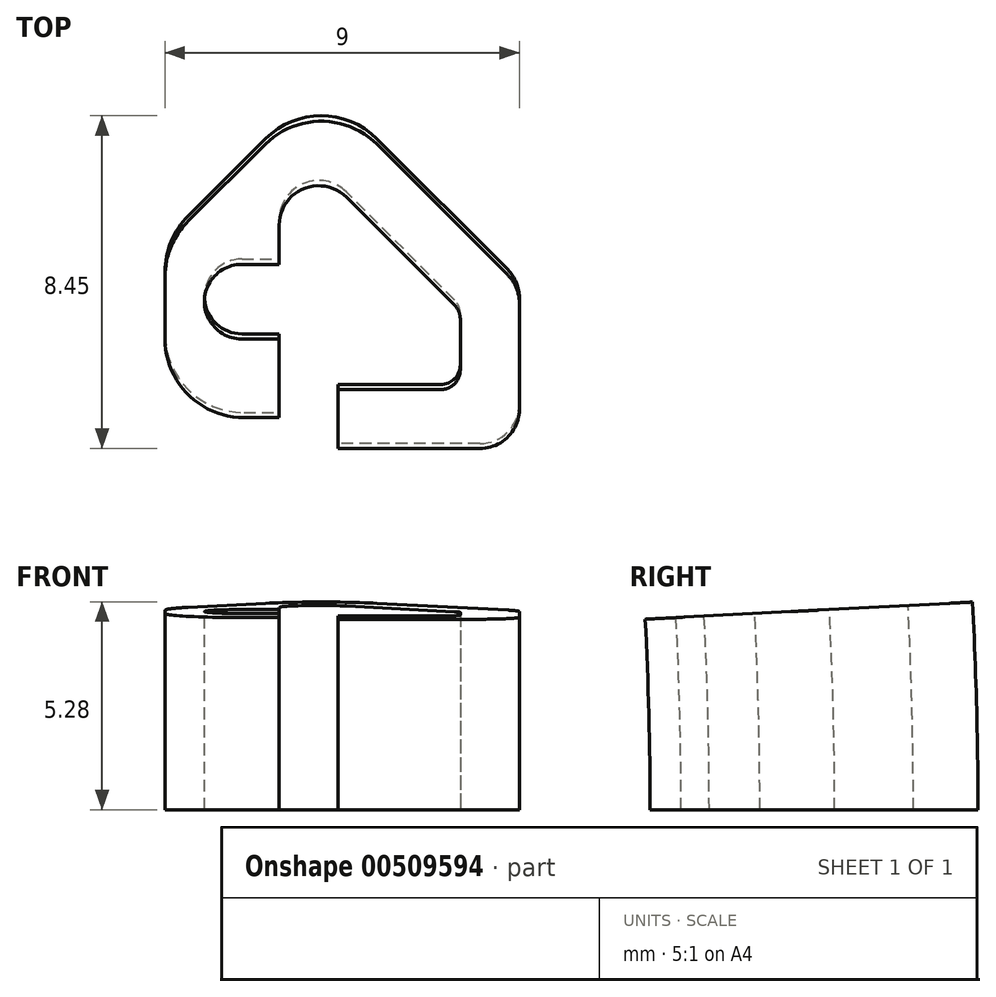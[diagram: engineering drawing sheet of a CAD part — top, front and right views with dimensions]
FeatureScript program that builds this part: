
annotation { "Feature Type Name" : "Feature", "Feature Type Description" : "" }
export const myFeature = defineFeature(function(context is Context, id is Id, definition is map)
    precondition{}
    {
        {
            var Q0;
            Q0=qCreatedBy(makeId("Top.planeOp"),FACE);
            var sketch = newSketch(context, id + "F0", { "sketchPlane" : qUnion([Q0])});
            skLineSegment(sketch, "E0", {"start": v(2.48, 100.21) * mm, "end": v(5.8, 96.89) * mm});
            skLineSegment(sketch, "E1", {"start": v(6.1, 96.18) * mm, "end": v(6.1, 93.47) * mm});
            skLineSegment(sketch, "E2", {"start": v(5.1, 92.47) * mm, "end": v(1.5, 92.47) * mm});
            skLineSegment(sketch, "E3", {"start": v(1.5, 92.47) * mm, "end": v(1.5, 93.97) * mm});
            skLineSegment(sketch, "E4", {"start": v(1.5, 93.97) * mm, "end": v(4.1, 93.97) * mm});
            skLineSegment(sketch, "E5", {"start": v(4.6, 94.47) * mm, "end": v(4.6, 95.77) * mm});
            skLineSegment(sketch, "E6", {"start": v(4.45, 96.12) * mm, "end": v(1.7, 98.87) * mm});
            skPoint(sketch, "E7.visualSharp", {"position": v(4.6, 93.97) * mm});
            skArc(sketch, "E7.filletArc", {"start": v(4.1, 93.97) * mm, "mid": v(4.45, 94.12) * mm, "end": v(4.6, 94.47) * mm});
            skPoint(sketch, "E8.visualSharp", {"position": v(4.6, 95.97) * mm});
            skArc(sketch, "E8.filletArc", {"start": v(4.6, 95.77) * mm, "mid": v(4.56, 95.96) * mm, "end": v(4.45, 96.12) * mm});
            skPoint(sketch, "E9.visualSharp", {"position": v(6.1, 92.47) * mm});
            skArc(sketch, "E9.filletArc", {"start": v(5.1, 92.47) * mm, "mid": v(5.8, 92.77) * mm, "end": v(6.1, 93.47) * mm});
            skPoint(sketch, "E10.visualSharp", {"position": v(6.1, 96.6) * mm});
            skArc(sketch, "E10.filletArc", {"start": v(6.1, 96.18) * mm, "mid": v(6.02, 96.56) * mm, "end": v(5.8, 96.89) * mm});
            skLineSegment(sketch, "E11", {"start": v(-2.9, 96.84) * mm, "end": v(-2.9, 95.26) * mm});
            skLineSegment(sketch, "E12", {"start": v(-0.9, 93.26) * mm, "end": v(0, 93.26) * mm});
            skLineSegment(sketch, "E13", {"start": v(0, 93.26) * mm, "end": v(0, 95.26) * mm});
            skArc(sketch, "E14", {"start": v(-0.95, 97.16) * mm, "mid": v(-1.9, 96.2) * mm, "end": v(-0.95, 95.26) * mm});
            skLineSegment(sketch, "E15", {"start": v(0, 97.16) * mm, "end": v(0, 95.26) * mm, "construction": true});
            skLineSegment(sketch, "E16", {"start": v(0, 95.26) * mm, "end": v(-0.95, 95.26) * mm});
            skPoint(sketch, "E17", {"position": v(-1.9, 96.2) * mm});
            skPoint(sketch, "E18.visualSharp", {"position": v(-2.9, 93.26) * mm});
            skArc(sketch, "E18.filletArc", {"start": v(-2.9, 95.26) * mm, "mid": v(-2.31, 93.85) * mm, "end": v(-0.9, 93.26) * mm});
            skPoint(sketch, "E19.visualSharp", {"position": v(-2.9, 102.7) * mm});
            skPoint(sketch, "E20.visualSharp", {"position": v(0, 102.7) * mm});
            skLineSegment(sketch, "E21", {"start": v(0, 0) * mm, "end": v(46.15, 0) * mm, "construction": true});
            skLineSegment(sketch, "E22", {"start": v(-0.95, 97.16) * mm, "end": v(0, 97.16) * mm});
            skLineSegment(sketch, "E23", {"start": v(0, 97.16) * mm, "end": v(0, 98.16) * mm});
            skPoint(sketch, "E24.visualSharp", {"position": v(0, 100.57) * mm});
            skArc(sketch, "E24.filletArc", {"start": v(1.7, 98.87) * mm, "mid": v(0.62, 99.08) * mm, "end": v(0, 98.16) * mm});
            skLineSegment(sketch, "E25", {"start": v(-0.35, 100.22) * mm, "end": v(-2.31, 98.26) * mm});
            skPoint(sketch, "E26.visualSharp", {"position": v(1.07, 101.63) * mm});
            skArc(sketch, "E26.filletArc", {"start": v(2.48, 100.21) * mm, "mid": v(1.07, 100.8) * mm, "end": v(-0.35, 100.22) * mm});
            skPoint(sketch, "E27.visualSharp", {"position": v(-2.9, 97.67) * mm});
            skArc(sketch, "E27.filletArc", {"start": v(-2.31, 98.26) * mm, "mid": v(-2.75, 97.6) * mm, "end": v(-2.9, 96.84) * mm});
            skLineSegment(sketch, "E28", {"start": v(0.51, 99.03) * mm, "end": v(-0.22, 100.34) * mm, "construction": true});
            skLineSegment(sketch, "E29", {"start": v(-1.49, 97) * mm, "end": v(-2.34, 98.23) * mm, "construction": true});
            skSolve(sketch);
        }
        {
            var Q0;
            Q0=makeQuery(id+"F0.imprint","IMPRINT",FACE,{"disambiguationData":[TD([[makeQuery(id+"F0.imprint","IMPRINT",EDGE,{"derivedFrom":sQuery(id+"F0.wireOp",EDGE,"E0")}),-1.0]])]});
            var Q1;
            Q1=sQuery(id+"F0.wireOp",EDGE,"E21");
            revolve(context, id + "F1", {"entities" : qUnion([Q0]), "axis" : qUnion([Q1]), "revolveType" : RevolveType.ONE_DIRECTION, "angle" : 3 * degree});
        }
    });
